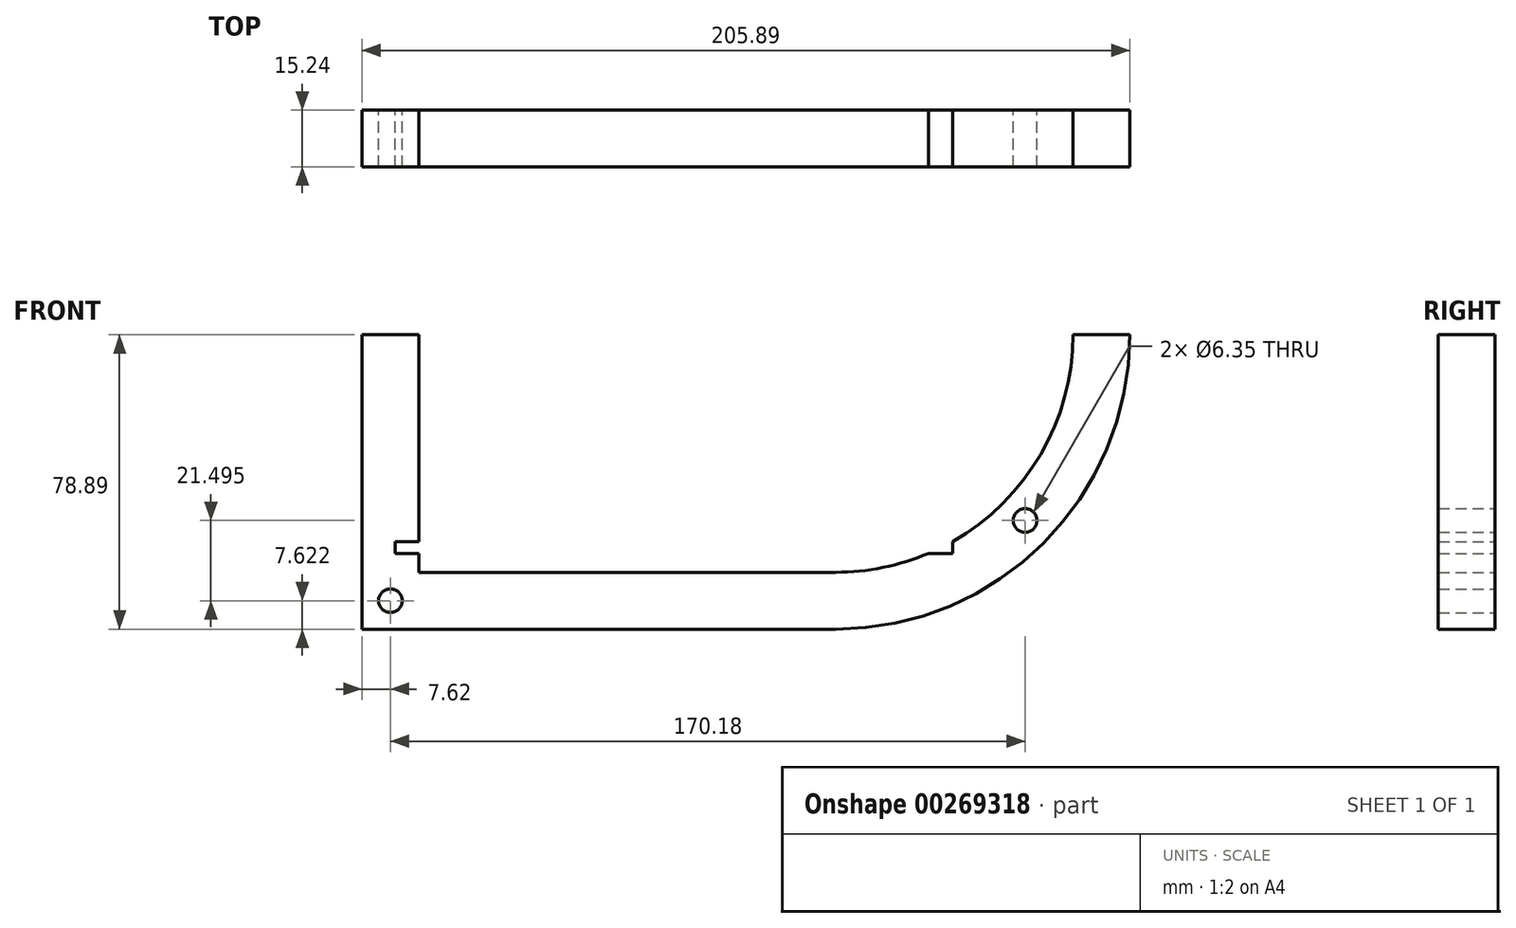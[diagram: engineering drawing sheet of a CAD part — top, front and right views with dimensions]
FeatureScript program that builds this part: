
annotation { "Feature Type Name" : "Feature", "Feature Type Description" : "" }
export const myFeature = defineFeature(function(context is Context, id is Id, definition is map)
    precondition{}
    {
        {
            var Q0;
            Q0=qCreatedBy(makeId("Front.planeOp"),FACE);
            var sketch = newSketch(context, id + "F0", { "sketchPlane" : qUnion([Q0])});
            skArc(sketch, "E0", {"start": v(0, -78.89) * mm, "mid": v(55.78, -55.78) * mm, "end": v(78.89, 0) * mm});
            skArc(sketch, "E1", {"start": v(0, -63.65) * mm, "mid": v(12.71, -62.37) * mm, "end": v(24.92, -58.57) * mm});
            skLineSegment(sketch, "E2", {"start": v(0, -78.89) * mm, "end": v(-127, -78.89) * mm});
            skLineSegment(sketch, "E3", {"start": v(-127, -78.89) * mm, "end": v(-127, 0) * mm});
            skLineSegment(sketch, "E4", {"start": v(-127, 0) * mm, "end": v(-111.76, 0) * mm});
            skLineSegment(sketch, "E5", {"start": v(0, -63.65) * mm, "end": v(-111.76, -63.65) * mm});
            skLineSegment(sketch, "E6", {"start": v(-111.76, -63.65) * mm, "end": v(-111.76, -58.57) * mm});
            skLineSegment(sketch, "E7", {"start": v(63.65, 0) * mm, "end": v(78.89, 0) * mm});
            skCircle(sketch, "E8", {"center": v(-119.38, -71.27) * mm, "radius": 3.18 * mm});
            skCircle(sketch, "E9", {"center": v(50.8, -49.77) * mm, "radius": 3.18 * mm});
            skLineSegment(sketch, "E10.bottom", {"start": v(-118.11, -58.57) * mm, "end": v(-111.76, -58.57) * mm});
            skLineSegment(sketch, "E10.top", {"start": v(-118.11, -55.4) * mm, "end": v(-111.76, -55.4) * mm});
            skLineSegment(sketch, "E10.left", {"start": v(-118.11, -58.57) * mm, "end": v(-118.11, -55.4) * mm});
            skLineSegment(sketch, "E10.right", {"start": v(31.35, -58.57) * mm, "end": v(31.35, -55.4) * mm});
            skLineSegment(sketch, "E11.trimOffspring", {"start": v(-111.76, -55.4) * mm, "end": v(-111.76, 0) * mm});
            skLineSegment(sketch, "E12.trimOffspring", {"start": v(24.92, -58.57) * mm, "end": v(31.35, -58.57) * mm});
            skArc(sketch, "E13.trimOffspring", {"start": v(31.35, -55.4) * mm, "mid": v(54.98, -32.06) * mm, "end": v(63.65, 0) * mm});
            skSolve(sketch);
        }
        {
            var Q0;
            Q0 = qSketchRegion(id + "F0", true);
            extrude(context, id + "F1", {"entities" : qUnion([Q0]), "depth" : 15.24 * mm});
        }
    });
